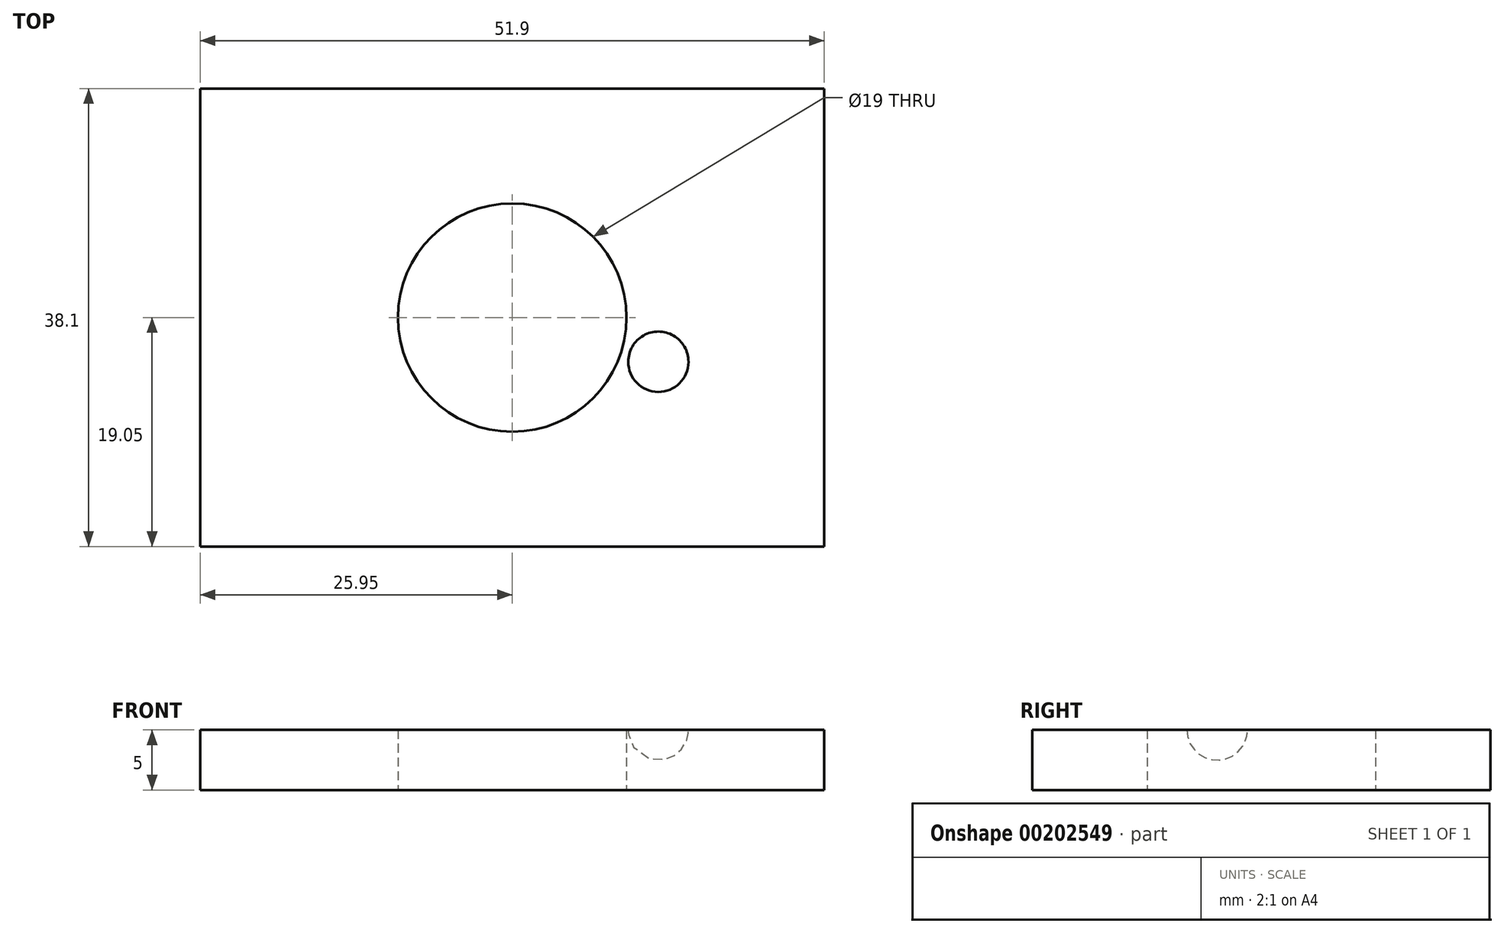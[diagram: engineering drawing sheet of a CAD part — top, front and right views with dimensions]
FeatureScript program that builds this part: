
annotation { "Feature Type Name" : "Feature", "Feature Type Description" : "" }
export const myFeature = defineFeature(function(context is Context, id is Id, definition is map)
    precondition{}
    {
        {
            var Q0;
            Q0=qCreatedBy(makeId("Top.planeOp"),FACE);
            var sketch = newSketch(context, id + "F0", { "sketchPlane" : qUnion([Q0])});
            skLineSegment(sketch, "E0.bottom", {"start": v(25.95, -19.05) * mm, "end": v(-25.95, -19.05) * mm});
            skLineSegment(sketch, "E0.top", {"start": v(25.95, 19.05) * mm, "end": v(-25.95, 19.05) * mm});
            skLineSegment(sketch, "E0.left", {"start": v(25.95, -19.05) * mm, "end": v(25.95, 19.05) * mm});
            skLineSegment(sketch, "E0.right", {"start": v(-25.95, -19.05) * mm, "end": v(-25.95, 19.05) * mm});
            skPoint(sketch, "E0.middle", {"position": v(0, 0) * mm});
            skCircle(sketch, "E1", {"center": v(0, 0) * mm, "radius": 9.5 * mm});
            skSolve(sketch);
        }
        {
            var Q0;
            Q0=makeQuery(id+"F0.imprint","IMPRINT",FACE,{"disambiguationData":[TD([[makeQuery(id+"F0.imprint","IMPRINT",EDGE,{"derivedFrom":sQuery(id+"F0.wireOp",EDGE,"E0.bottom")}),-1.0]])]});
            extrude(context, id + "F1", {"entities" : qUnion([Q0]), "endBound" : BoundingType.SYMMETRIC, "depth" : 5 * mm});
        }
        {
            var Q0;
            Q0=makeQuery(id+"F1.opExtrude","CAP_FACE",FACE,{"disambiguationData":[OSD([sQuery(id+"F0.wireOp",EDGE,"E0.bottom"),sQuery(id+"F0.wireOp",EDGE,"E0.top"),sQuery(id+"F0.wireOp",EDGE,"E0.left"),sQuery(id+"F0.wireOp",EDGE,"E0.right"),sQuery(id+"F0.wireOp",EDGE,"E1")])],"isStart":false});
            var sketch = newSketch(context, id + "F2", { "sketchPlane" : qUnion([Q0])});
            skCircle(sketch, "E2", {"center": v(0, 0) * mm, "radius": 12.7 * mm});
            skCircle(sketch, "E3", {"center": v(0, 12.7) * mm, "radius": 2.5 * mm, "construction": true});
            skCircle(sketch, "E4", {"center": v(12.15, -3.69) * mm, "radius": 2.5 * mm});
            skCircle(sketch, "E5.MirrorC", {"center": v(0, 0) * mm, "radius": 12.7 * mm, "construction": true});
            skCircle(sketch, "E6.MirrorC", {"center": v(-12.15, -3.69) * mm, "radius": 2.5 * mm, "construction": true});
            skLineSegment(sketch, "E7", {"start": v(9.65, -3.66) * mm, "end": v(14.65, -3.69) * mm});
            skLineSegment(sketch, "E8.bottom", {"start": v(-7.2, -6.19) * mm, "end": v(-19.24, -6.19) * mm});
            skLineSegment(sketch, "E8.top", {"start": v(-7.2, -1.19) * mm, "end": v(-19.24, -1.19) * mm});
            skLineSegment(sketch, "E8.left", {"start": v(-7.2, -6.19) * mm, "end": v(-7.2, -1.19) * mm});
            skLineSegment(sketch, "E8.right", {"start": v(-19.24, -6.19) * mm, "end": v(-19.24, -1.19) * mm});
            skSolve(sketch);
        }
        {
            var Q0;
            {var subQ0=sQuery(id+"F2.wireOp",EDGE,"E4");var subQ1=sQuery(id+"F2.wireOp",EDGE,"E2");var subQ2=makeQuery(id+"F2.imprint","INTERSECT",VERTEX,{"disambiguationData":[OD(0.0)],"derivedFrom":[subQ1,subQ0]});Q0=makeQuery(id+"F2.imprint","IMPRINT",FACE,{"disambiguationData":[TD([[makeQuery(id+"F2.imprint","IMPRINT",EDGE,{"disambiguationData":[TD([[subQ2,-1.0]])],"derivedFrom":subQ1}),1.0]])]});}
            var Q1;
            {var subQ0=sQuery(id+"F2.wireOp",EDGE,"E4");var subQ1=sQuery(id+"F2.wireOp",EDGE,"E2");var subQ2=makeQuery(id+"F2.imprint","INTERSECT",VERTEX,{"disambiguationData":[OD(0.0)],"derivedFrom":[subQ1,subQ0]});Q1=makeQuery(id+"F2.imprint","IMPRINT",FACE,{"disambiguationData":[TD([[makeQuery(id+"F2.imprint","IMPRINT",EDGE,{"disambiguationData":[TD([[subQ2,-1.0]])],"derivedFrom":subQ1}),-1.0]])]});}
            var Q2;
            Q2=sQuery(id+"F2.wireOp",EDGE,"E7");
            revolve(context, id + "F3", {"operationType" : NewBodyOperationType.REMOVE, "entities" : qUnion([Q0, Q1]), "axis" : qUnion([Q2]), "revolveType" : RevolveType.FULL, "oppositeDirection" : true});
        }
    });
